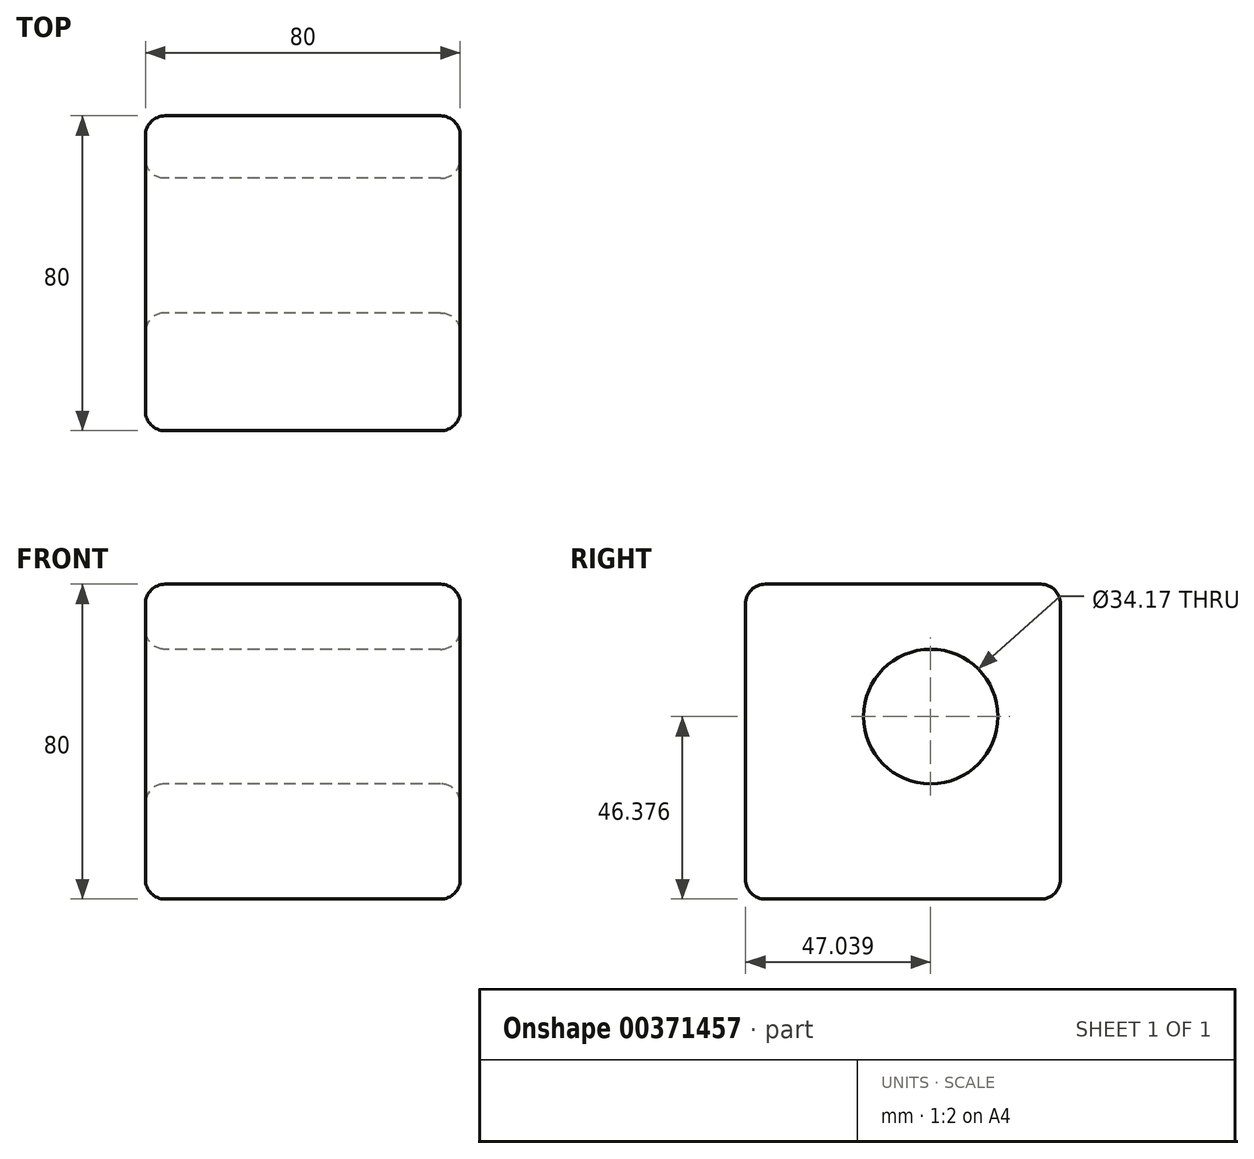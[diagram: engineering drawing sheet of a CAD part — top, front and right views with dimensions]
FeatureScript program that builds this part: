
annotation { "Feature Type Name" : "Feature", "Feature Type Description" : "" }
export const myFeature = defineFeature(function(context is Context, id is Id, definition is map)
    precondition{}
    {
        {
            var Q0;
            Q0=qCreatedBy(makeId("Top.planeOp"),FACE);
            var sketch = newSketch(context, id + "F0", { "sketchPlane" : qUnion([Q0])});
            skLineSegment(sketch, "E0.bottom", {"start": v(-37.8, 49.6) * mm, "end": v(42.2, 49.6) * mm});
            skLineSegment(sketch, "E0.top", {"start": v(-37.8, -30.4) * mm, "end": v(42.2, -30.4) * mm});
            skLineSegment(sketch, "E0.left", {"start": v(-37.8, 49.6) * mm, "end": v(-37.8, -30.4) * mm});
            skLineSegment(sketch, "E0.right", {"start": v(42.2, 49.6) * mm, "end": v(42.2, -30.4) * mm});
            skSolve(sketch);
        }
        {
            var Q0;
            Q0 = qSketchRegion(id + "F0", true);
            extrude(context, id + "F1", {"entities" : qUnion([Q0]), "depth" : 80 * mm});
        }
        {
            var Q0;
            Q0=makeQuery(id+"F1.opExtrude","SWEPT_FACE",FACE,{"disambiguationData":[OSD([sQuery(id+"F0.wireOp",EDGE,"E0.left")])]});
            var sketch = newSketch(context, id + "F2", { "sketchPlane" : qUnion([Q0])});
            skCircle(sketch, "E1", {"center": v(-16.63, 46.38) * mm, "radius": 17.09 * mm});
            skSolve(sketch);
        }
        {
            var Q0;
            Q0=makeQuery(id+"F2.imprint","IMPRINT",FACE,{"disambiguationData":[TD([[makeQuery(id+"F2.imprint","IMPRINT",EDGE,{"derivedFrom":sQuery(id+"F2.wireOp",EDGE,"E1")}),1.0]])]});
            extrude(context, id + "F3", {"entities" : qUnion([Q0]), "operationType" : NewBodyOperationType.REMOVE, "endBound" : BoundingType.THROUGH_ALL, "oppositeDirection" : true, "depth" : 25 * mm});
        }
        {
            var Q0;
            Q0=makeQuery(id+"F1.opExtrude","SWEPT_EDGE",EDGE,{"disambiguationData":[OSD([sQuery(id+"F0.wireOp",EDGE,"E0.bottom"),sQuery(id+"F0.wireOp",EDGE,"E0.left")])]});
            var Q1;
            Q1=makeQuery(id+"F1.opExtrude","CAP_EDGE",EDGE,{"disambiguationData":[OSD([sQuery(id+"F0.wireOp",EDGE,"E0.left")])],"isStart":false});
            var Q2;
            Q2=makeQuery(id+"F1.opExtrude","SWEPT_EDGE",EDGE,{"disambiguationData":[OSD([sQuery(id+"F0.wireOp",EDGE,"E0.top"),sQuery(id+"F0.wireOp",EDGE,"E0.left")])]});
            var Q3;
            Q3=makeQuery(id+"F1.opExtrude","SWEPT_FACE",FACE,{"disambiguationData":[OSD([sQuery(id+"F0.wireOp",EDGE,"E0.left")])]});
            var Q4;
            Q4=makeQuery(id+"F1.opExtrude","SWEPT_FACE",FACE,{"disambiguationData":[OSD([sQuery(id+"F0.wireOp",EDGE,"E0.bottom")])]});
            var Q5;
            Q5=makeQuery(id+"F1.opExtrude","CAP_EDGE",EDGE,{"disambiguationData":[OSD([sQuery(id+"F0.wireOp",EDGE,"E0.bottom")])],"isStart":false});
            var Q6;
            Q6=makeQuery(id+"F1.opExtrude","SWEPT_EDGE",EDGE,{"disambiguationData":[OSD([sQuery(id+"F0.wireOp",EDGE,"E0.bottom"),sQuery(id+"F0.wireOp",EDGE,"E0.right")])]});
            var Q7;
            Q7=makeQuery(id+"F1.opExtrude","SWEPT_EDGE",EDGE,{"disambiguationData":[OSD([sQuery(id+"F0.wireOp",EDGE,"E0.top"),sQuery(id+"F0.wireOp",EDGE,"E0.right")])]});
            var Q8;
            Q8=makeQuery(id+"F1.opExtrude","CAP_EDGE",EDGE,{"disambiguationData":[OSD([sQuery(id+"F0.wireOp",EDGE,"E0.right")])],"isStart":false});
            var Q9;
            Q9=makeQuery(id+"F1.opExtrude","SWEPT_FACE",FACE,{"disambiguationData":[OSD([sQuery(id+"F0.wireOp",EDGE,"E0.right")])]});
            var Q10;
            Q10=makeQuery(id+"F1.opExtrude","SWEPT_FACE",FACE,{"disambiguationData":[OSD([sQuery(id+"F0.wireOp",EDGE,"E0.top")])]});
            var Q11;
            Q11=makeQuery(id+"F1.opExtrude","CAP_EDGE",EDGE,{"disambiguationData":[OSD([sQuery(id+"F0.wireOp",EDGE,"E0.top")])],"isStart":false});
            fillet(context, id + "F4", {"entities" : qUnion([Q0, Q1, Q2, Q3, Q4, Q5, Q6, Q7, Q8, Q9, Q10, Q11]), "radius" : 5 * mm, "tangentPropagation" : true, "allowEdgeOverflow" : false});
        }
    });
